# Revit family: BISLEY_SystemFile_Two_Door_Cupboards
name_source: partatom
category: Furniture
revit_build: Autodesk Revit 2018 (Build: 20180423_1000(x64)
units: mm (PartAtom-declared; Revit-internal decimal feet)

## family parameters
Always vertical = Yes
Cut with Voids When Loaded = No
OmniClass Number = 23.40.20.00
OmniClass Title = General Furniture and Specialties
Room Calculation Point = No
Shared = No
Work Plane-Based = No

## types (16) — shared parameters
Category = Cupboard
Compliance Standards Certification = BS EN 14073 2004 Part 2 & 3, BS EN 14074, BS 4875 1998 Part 7 level 4 & Part 8, BS 476 Part 7 1987 Class 2Y
Depth = 470 mm  [stored 1.54199 ft]
Description = Two Door Cupboard
Finish = Powder Coated
Manufacturer = Bisley
Material = Steel
Product Information = Furniture
Range = SystemFile
Routine Maintenance = We recommend you clean your unit with warm water and a mild detergent solution. A damp cloth can be used to remove dust particles.
Uniclass 2015 Code = PR_40_30_57
Warranty = 10 years

## per-type parameters (varying)
| type | Height | Model Reference | URL | Width |
| SYD08/2 | 693 mm  [stored 2.27362 ft] | SYD08/2 | www.bisley.com | 800 mm  [stored 2.62467 ft] |
| SYD08/3 | 997 mm | STD08/3 | www.bisley.com | 800 mm  [stored 2.62467 ft] |
| SYD08/34 | 1149 mm  [stored 3.76969 ft] | SYC08/34 | www.bisley.com | 800 mm  [stored 2.62467 ft] |
| SYD08/4 | 1301 mm  [stored 4.26837 ft] | SYD08/4 | www.bisley.com | 800 mm  [stored 2.62467 ft] |
| SYD08/43 | 1415 mm  [stored 4.64239 ft] | SYD08/43 | www.bisley.com | 800 mm  [stored 2.62467 ft] |
| SYD08/50 | 1643 mm  [stored 5.39042 ft] | SYD08/50 | www.Bisley.com | 800 mm  [stored 2.62467 ft] |
| SYD08/54 | 1795 mm | SYD08/54 | www.bisley.com | 800 mm  [stored 2.62467 ft] |
| SYD08/6 | 1947 mm  [stored 6.3878 ft] | SYC08/6 | www.bisley.com | 800 mm  [stored 2.62467 ft] |
| SYD10/2 | 693 mm  [stored 2.27362 ft] | SYD10/2 | www.bisley.com | 1000 mm  [stored 3.28084 ft] |
| SYD10/3 | 997 mm | SYD10/3 | www.bisley.com | 1000 mm  [stored 3.28084 ft] |
| SYD10/34 | 1149 mm  [stored 3.76969 ft] | SYD10/34 | www.bisley.com | 1000 mm  [stored 3.28084 ft] |
| SYD10/4 | 1301 mm  [stored 4.26837 ft] | SYD10/4 | www.bisley.com | 1000 mm  [stored 3.28084 ft] |
| SYD10/43 | 1415 mm  [stored 4.64239 ft] | SYD10/43 | www.bisley.com | 1000 mm  [stored 3.28084 ft] |
| SYD10/50 | 1643 mm  [stored 5.39042 ft] | SYD10/50 | www.bisley.com | 1000 mm  [stored 3.28084 ft] |
| SYD10/54 | 1795 mm | SYD10/54 | www.bisley.com | 1000 mm  [stored 3.28084 ft] |
| SYD10/6 | 1947 mm  [stored 6.3878 ft] | SYD10/6 | www.bisley.com | 1000 mm  [stored 3.28084 ft] |

note: [stored X ft] marks values corroborated as IEEE doubles in the binary element streams (Revit-internal decimal feet)

## geometry (parser evidence)
native form markers: Sweep x3
no freeform markers — native parametric forms only
